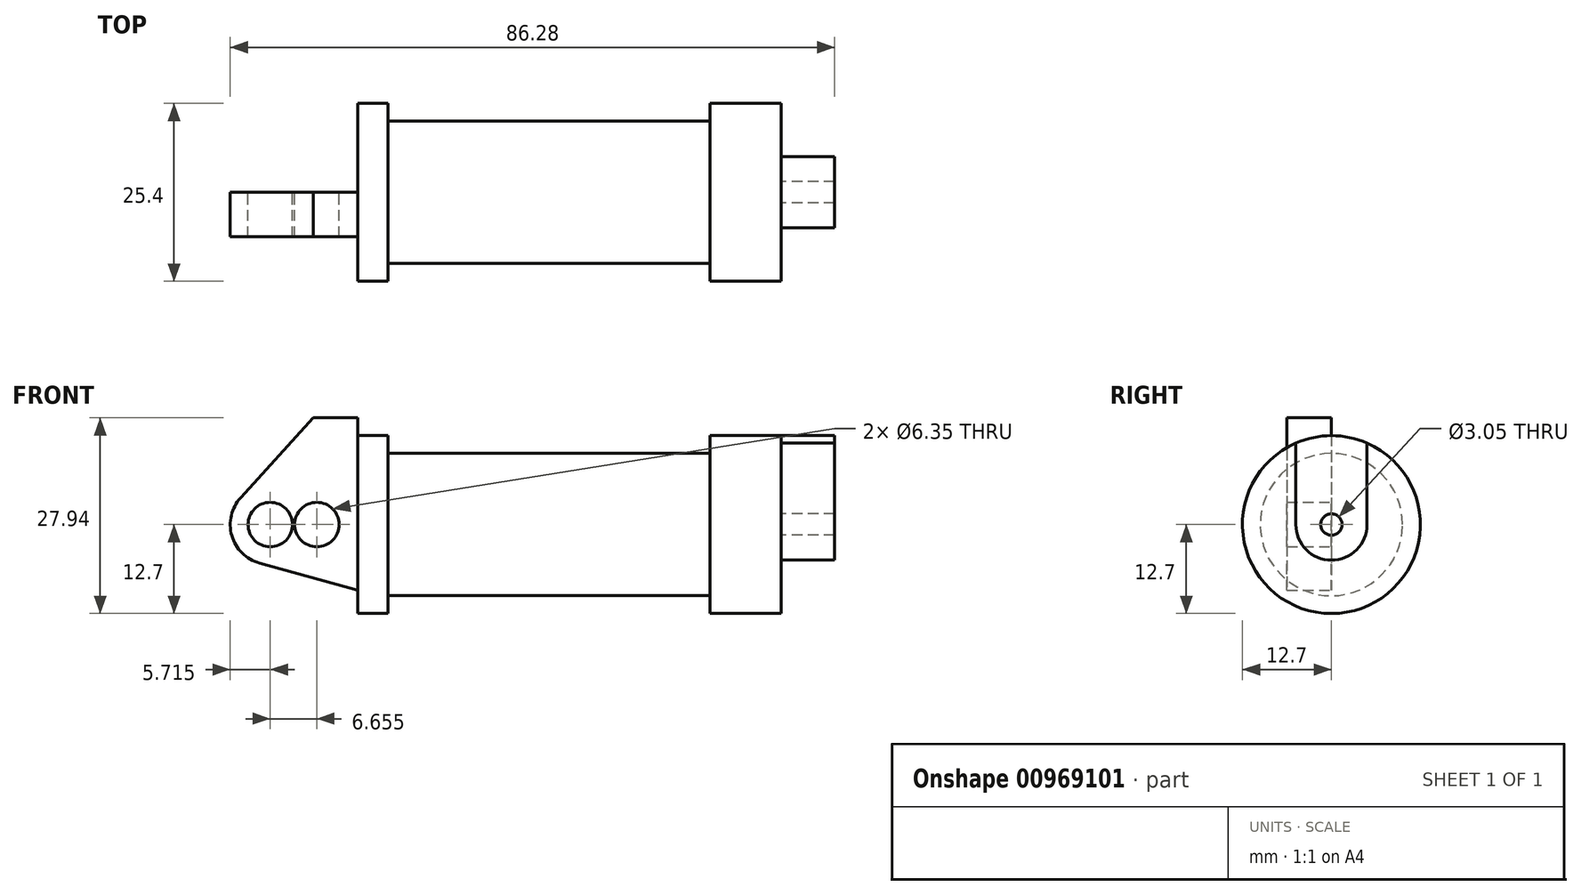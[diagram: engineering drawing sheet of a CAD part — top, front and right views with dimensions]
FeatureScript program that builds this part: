
annotation { "Feature Type Name" : "Feature", "Feature Type Description" : "" }
export const myFeature = defineFeature(function(context is Context, id is Id, definition is map)
    precondition{}
    {
        {
            var Q0;
            Q0=qCreatedBy(makeId("Front.planeOp"),FACE);
            var sketch = newSketch(context, id + "F0", { "sketchPlane" : qUnion([Q0])});
            skLineSegment(sketch, "E0", {"start": v(0, 0) * mm, "end": v(0, 12.7) * mm});
            skLineSegment(sketch, "E1", {"start": v(0, 12.7) * mm, "end": v(10.16, 12.7) * mm});
            skLineSegment(sketch, "E2", {"start": v(10.16, 12.7) * mm, "end": v(10.16, 10.16) * mm});
            skLineSegment(sketch, "E3", {"start": v(10.16, 10.16) * mm, "end": v(56.13, 10.16) * mm});
            skLineSegment(sketch, "E4", {"start": v(56.13, 10.16) * mm, "end": v(56.13, 12.7) * mm});
            skLineSegment(sketch, "E5", {"start": v(56.13, 12.7) * mm, "end": v(66.3, 12.7) * mm});
            skLineSegment(sketch, "E6", {"start": v(66.3, 12.7) * mm, "end": v(66.3, 0) * mm});
            skLineSegment(sketch, "E7", {"start": v(66.3, 0) * mm, "end": v(0, 0) * mm});
            skLineSegment(sketch, "E8", {"start": v(5.84, 15.24) * mm, "end": v(-0.5, 15.24) * mm});
            skLineSegment(sketch, "E9", {"start": v(-0.5, 15.24) * mm, "end": v(-10.88, 3.85) * mm});
            skLineSegment(sketch, "E10", {"start": v(0, 0) * mm, "end": v(-6.65, 0) * mm});
            skCircle(sketch, "E11", {"center": v(-6.65, 0) * mm, "radius": 5.72 * mm});
            skCircle(sketch, "E12", {"center": v(-6.65, 0) * mm, "radius": 3.18 * mm});
            skLineSegment(sketch, "E13", {"start": v(5.84, 15.24) * mm, "end": v(5.84, -9.4) * mm});
            skLineSegment(sketch, "E14", {"start": v(5.84, -9.4) * mm, "end": v(-8.18, -5.5) * mm});
            skSolve(sketch);
        }
        {
            var Q0;
            {var subQ0=sQuery(id+"F0.wireOp",EDGE,"E2");Q0=makeQuery(id+"F0.imprint","IMPRINT",FACE,{"disambiguationData":[TD([[makeQuery(id+"F0.imprint","IMPRINT",EDGE,{"derivedFrom":subQ0}),-1.0]])]});}
            var Q1;
            Q1=sQuery(id+"F0.wireOp",EDGE,"E7");
            revolve(context, id + "F1", {"surfaceOperationType" : NewSurfaceOperationType.NEW, "entities" : qUnion([Q0]), "axis" : qUnion([Q1]), "revolveType" : RevolveType.FULL});
        }
        {
            var Q0;
            {var subQ1=sQuery(id+"F0.wireOp",EDGE,"E0");Q0=makeQuery(id+"F0.imprint","IMPRINT",FACE,{"disambiguationData":[TD([[makeQuery(id+"F0.imprint","IMPRINT",EDGE,{"derivedFrom":subQ1}),1.0]])]});}
            var Q1;
            {var subQ0=sQuery(id+"F0.wireOp",EDGE,"E14");Q1=makeQuery(id+"F0.imprint","IMPRINT",FACE,{"disambiguationData":[TD([[makeQuery(id+"F0.imprint","IMPRINT",EDGE,{"derivedFrom":subQ0}),-1.0]])]});}
            var Q2;
            {var subQ5=sQuery(id+"F0.wireOp",EDGE,"E12");Q2=makeQuery(id+"F0.imprint","IMPRINT",FACE,{"disambiguationData":[TD([[makeQuery(id+"F0.imprint","IMPRINT",EDGE,{"derivedFrom":subQ5}),-1.0]])]});}
            var Q3;
            {var subQ0=sQuery(id+"F0.wireOp",EDGE,"E0");Q3=makeQuery(id+"F0.imprint","IMPRINT",FACE,{"disambiguationData":[TD([[makeQuery(id+"F0.imprint","IMPRINT",EDGE,{"derivedFrom":subQ0}),-1.0]])]});}
            extrude(context, id + "F2", {"entities" : qUnion([Q0, Q1, Q2, Q3]), "operationType" : NewBodyOperationType.ADD, "depth" : 6.35 * mm, "offsetDistance" : 25.4 * mm});
        }
        {
            var Q0;
            Q0=makeQuery(id+"F1.opRevolve","SWEPT_FACE",FACE,{"disambiguationData":[OSD([sQuery(id+"F0.wireOp",EDGE,"E6")])]});
            var sketch = newSketch(context, id + "F3", { "sketchPlane" : qUnion([Q0])});
            skCircle(sketch, "E15", {"center": v(0, 0) * mm, "radius": 1.52 * mm});
            skCircle(sketch, "E16", {"center": v(0, 0) * mm, "radius": 5.08 * mm});
            skLineSegment(sketch, "E17", {"start": v(5.08, 0) * mm, "end": v(5.08, 15.24) * mm});
            skLineSegment(sketch, "E18", {"start": v(-5.08, 0) * mm, "end": v(-5.08, 15.24) * mm});
            skLineSegment(sketch, "E19", {"start": v(5.08, 15.24) * mm, "end": v(-5.08, 15.24) * mm});
            skSolve(sketch);
        }
        {
            var Q0;
            Q0=makeQuery(id+"F3.imprint","IMPRINT",FACE,{"disambiguationData":[TD([[makeQuery(id+"F3.imprint","IMPRINT",EDGE,{"derivedFrom":sQuery(id+"F3.wireOp",EDGE,"E15")}),-1.0]])]});
            var Q1;
            {var subQ0=sQuery(id+"F3.wireOp",EDGE,"E17");var subQ1=sQuery(id+"F3.wireOp",EDGE,"E16");var subQ2=makeQuery(id+"F3.imprint","INTERSECT",VERTEX,{"derivedFrom":[subQ1,subQ0]});Q1=makeQuery(id+"F3.imprint","IMPRINT",FACE,{"disambiguationData":[TD([[makeQuery(id+"F3.imprint","IMPRINT",EDGE,{"disambiguationData":[TD([[subQ2,-1.0]])],"derivedFrom":subQ1}),-1.0]])]});}
            extrude(context, id + "F4", {"entities" : qUnion([Q0, Q1]), "depth" : 7.62 * mm, "offsetDistance" : 25.4 * mm});
        }
        {
            var Q0;
            Q0=sQuery(id+"F0.wireOp",VERTEX,"E0.start");
            var Q1;
            Q1=makeQuery(id+"F1.opRevolve","SWEPT_BODY",BODY,{"disambiguationData":[OSD([sQuery(id+"F0.wireOp",EDGE,"E1"),sQuery(id+"F0.wireOp",EDGE,"E2"),sQuery(id+"F0.wireOp",EDGE,"E3"),sQuery(id+"F0.wireOp",EDGE,"E4"),sQuery(id+"F0.wireOp",EDGE,"E5"),sQuery(id+"F0.wireOp",EDGE,"E6"),sQuery(id+"F0.wireOp",EDGE,"E7"),sQuery(id+"F0.wireOp",EDGE,"E13")])]});
            hole(context, id + "F5", {"style" : HoleStyle.SIMPLE, "endStyle" : HoleEndStyle.THROUGH, "oppositeDirection" : true, "holeDiameter" : 6.35 * mm, "majorDiameter" : 6.35 * mm, "isTappedThrough" : true, "tappedDepth" : 12.7 * mm, "tapClearance" : 3, "locations" : qUnion([Q0]), "scope" : qUnion([Q1])});
        }
    });
